# Revit family: Louver-Penthouse-Carnes-Mitered_Corner-PMAB
name_source: partatom
category: Air Terminals
revit_build: Autodesk Revit Architecture 2012 (Build: 20110916_2132(x64)
units: mm (PartAtom-declared; Revit-internal decimal feet)

## types (361) — shared parameters
04 CSI = 08 91 00
1 In 12 Pitched Roof = No
3 in 12 Pitched Roof = Yes
95 CSI = 10200
Assembly Code = D3090700
Blade Material = Aluminum - Carnes - Extruded
Catalog URL = http://www.carnes.com
Connector Description 1 = Duct Connection 1
Custom Length = 220"
Description = Extruded Aluminum Penthouses
Flat Roof = No
Frame Material = Aluminum - Carnes - Extruded
Manufacturer = Carnes Company
Manufacturer Fax = 608-845-6470
Model = PMBA
Pitched Roof Visibility = Yes
Pressure Drop = 0.00 Pa
Product Line = Extruded Aluminum Penthouses
Product Page URL = http://www.carnes.com
Rectangular Length = No
Roof Pitch = 14.04°
Specifications  URL = http://www.carnes.com
Subcategory = Louvers and Dampers
URL = http://www.carnes.com
ecoScorecard Product Page = http://ecoscorecard.com

## per-type parameters (varying)
| type | Blades Length | Blades Quantity | Blades Quantity Control | Blades Width | Free Area | Length Control | Louver Height | Louver Length | Louver Width |
| 12 W x 12 H | 15" | 2 | 2 | 15" | 0.19 SF | 12" | 12" | 12" | 12" |
| 12 W x 18 H | 15" | 4 | 3 | 15" | 0.5 SF | 12" | 18" | 12" | 12" |
| 12 W x 24 H | 15" | 5 | 4 | 15" | 0.77 SF | 12" | 24" | 12" | 12" |
| 12 W x 30 H | 15" | 6 | 5 | 15" | 0.96 SF | 12" | 30" | 12" | 12" |
| 12 W x 36 H | 15" | 7 | 7 | 15" | 1.15 SF | 12" | 36" | 12" | 12" |
| 12 W x 42 H | 15" | 9 | 8 | 15" | 1.43 SF | 12" | 42" | 12" | 12" |
| 12 W x 48 H | 15" | 10 | 9 | 15" | 1.61 SF | 12" | 48" | 12" | 12" |
| 12 W x 54 H | 15" | 11 | 11 | 15" | 1.92 SF | 12" | 54" | 12" | 12" |
| 12 W x 60 H | 15" | 13 | 12 | 15" | 2.11 SF | 12" | 60" | 12" | 12" |
| 12 W x 66 H | 15" | 14 | 13 | 15" | 2.35 SF | 12" | 66" | 12" | 12" |
| 12 W x 72 H | 15" | 15 | 15 | 15" | 2.81 SF | 12" | 72" | 12" | 12" |
| 12 W x 78 H | 15" | 17 | 16 | 15" | 2.88 SF | 12" | 78" | 12" | 12" |
| 12 W x 84 H | 15" | 18 | 17 | 15" | 3.07 SF | 12" | 84" | 12" | 12" |
| 12 W x 90 H | 15" | 19 | 18 | 15" | 3.28 SF | 12" | 90" | 12" | 12" |
| 12 W x 96 H | 15" | 20 | 20 | 15" | 3.55 SF | 12" | 96" | 12" | 12" |
| 12 W x 102 H | 15" | 22 | 21 | 15" | 3.82 SF | 12" | 102" | 12" | 12" |
| 12 W x 108 H | 15" | 23 | 22 | 15" | 3.96 SF | 12" | 108" | 12" | 12" |
| 12 W x 114 H | 15" | 24 | 24 | 15" | 4.24 SF | 12" | 114" | 12" | 12" |
| 12 W x 120 H | 15" | 26 | 25 | 15" | 4.28 SF | 12" | 120" | 12" | 12" |
| 18 W x 12 H | 21" | 2 | 2 | 21" | 0.31 SF | 18" | 12" | 18" | 18" |
| 18 W x 18 H | 21" | 4 | 3 | 21" | 0.8 SF | 18" | 18" | 18" | 18" |
| 18 W x 24 H | 21" | 5 | 4 | 21" | 1.23 SF | 18" | 24" | 18" | 18" |
| 18 W x 30 H | 21" | 6 | 5 | 21" | 1.54 SF | 18" | 30" | 18" | 18" |
| 18 W x 36 H | 21" | 7 | 7 | 21" | 1.85 SF | 18" | 36" | 18" | 18" |
| 18 W x 42 H | 21" | 9 | 8 | 21" | 2.29 SF | 18" | 42" | 18" | 18" |
| 18 W x 48 H | 21" | 10 | 9 | 21" | 2.59 SF | 18" | 48" | 18" | 18" |
| 18 W x 54 H | 21" | 11 | 11 | 21" | 3.09 SF | 18" | 54" | 18" | 18" |
| 18 W x 60 H | 21" | 13 | 12 | 21" | 3.4 SF | 18" | 60" | 18" | 18" |
| 18 W x 66 H | 21" | 14 | 13 | 21" | 3.78 SF | 18" | 66" | 18" | 18" |
| 18 W x 72 H | 21" | 15 | 15 | 21" | 4.52 SF | 18" | 72" | 18" | 18" |
| 18 W x 78 H | 21" | 17 | 16 | 21" | 4.63 SF | 18" | 78" | 18" | 18" |
| 18 W x 84 H | 21" | 18 | 17 | 21" | 4.94 SF | 18" | 84" | 18" | 18" |
| 18 W x 90 H | 21" | 19 | 18 | 21" | 5.27 SF | 18" | 90" | 18" | 18" |
| 18 W x 96 H | 21" | 20 | 20 | 21" | 5.7 SF | 18" | 96" | 18" | 18" |
| 18 W x 102 H | 21" | 22 | 21 | 21" | 6.13 SF | 18" | 102" | 18" | 18" |
| 18 W x 108 H | 21" | 23 | 22 | 21" | 6.37 SF | 18" | 108" | 18" | 18" |
| 18 W x 114 H | 21" | 24 | 24 | 21" | 6.81 SF | 18" | 114" | 18" | 18" |
| 18 W x 120 H | 21" | 26 | 25 | 21" | 6.89 SF | 18" | 120" | 18" | 18" |
| 24 W x 12 H | 27" | 2 | 2 | 27" | 0.43 SF | 24" | 12" | 24" | 24" |
| 24 W x 18 H | 27" | 4 | 3 | 27" | 1.1 SF | 24" | 18" | 24" | 24" |
| 24 W x 24 H | 27" | 5 | 4 | 27" | 1.7 SF | 24" | 24" | 24" | 24" |
| 24 W x 30 H | 27" | 6 | 5 | 27" | 2.13 SF | 24" | 30" | 24" | 24" |
| 24 W x 36 H | 27" | 7 | 7 | 27" | 2.55 SF | 24" | 36" | 24" | 24" |
| 24 W x 42 H | 27" | 9 | 8 | 27" | 3.16 SF | 24" | 42" | 24" | 24" |
| 24 W x 48 H | 27" | 10 | 9 | 27" | 3.57 SF | 24" | 48" | 24" | 24" |
| 24 W x 54 H | 27" | 11 | 11 | 27" | 4.26 SF | 24" | 54" | 24" | 24" |
| 24 W x 60 H | 27" | 13 | 12 | 27" | 4.68 SF | 24" | 60" | 24" | 24" |
| 24 W x 66 H | 27" | 14 | 13 | 27" | 5.21 SF | 24" | 66" | 24" | 24" |
| 24 W x 72 H | 27" | 15 | 15 | 27" | 6.23 SF | 24" | 72" | 24" | 24" |
| 24 W x 78 H | 27" | 17 | 16 | 27" | 6.39 SF | 24" | 78" | 24" | 24" |
| 24 W x 84 H | 27" | 18 | 17 | 27" | 6.81 SF | 24" | 84" | 24" | 24" |
| 24 W x 90 H | 27" | 19 | 18 | 27" | 7.27 SF | 24" | 90" | 24" | 24" |
| 24 W x 96 H | 27" | 20 | 20 | 27" | 7.86 SF | 24" | 96" | 24" | 24" |
| 24 W x 102 H | 27" | 22 | 21 | 27" | 8.45 SF | 24" | 102" | 24" | 24" |
| 24 W x 108 H | 27" | 23 | 22 | 27" | 8.78 SF | 24" | 108" | 24" | 24" |
| 24 W x 114 H | 27" | 24 | 24 | 27" | 9.38 SF | 24" | 114" | 24" | 24" |
| 24 W x 120 H | 27" | 26 | 25 | 27" | 9.49 SF | 24" | 120" | 24" | 24" |
| 30 W x 12 H | 33" | 2 | 2 | 33" | 0.54 SF | 30" | 12" | 30" | 30" |
| 30 W x 18 H | 33" | 4 | 3 | 33" | 1.41 SF | 30" | 18" | 30" | 30" |
| 30 W x 24 H | 33" | 5 | 4 | 33" | 2.16 SF | 30" | 24" | 30" | 30" |
| 30 W x 30 H | 33" | 6 | 5 | 33" | 2.71 SF | 30" | 30" | 30" | 30" |
| 30 W x 36 H | 33" | 7 | 7 | 33" | 3.25 SF | 30" | 36" | 30" | 30" |
| 30 W x 42 H | 33" | 9 | 8 | 33" | 4.02 SF | 30" | 42" | 30" | 30" |
| 30 W x 48 H | 33" | 10 | 9 | 33" | 4.55 SF | 30" | 48" | 30" | 30" |
| 30 W x 54 H | 33" | 11 | 11 | 33" | 5.42 SF | 30" | 54" | 30" | 30" |
| 30 W x 60 H | 33" | 13 | 12 | 33" | 5.97 SF | 30" | 60" | 30" | 30" |
| 30 W x 66 H | 33" | 14 | 13 | 33" | 6.64 SF | 30" | 66" | 30" | 30" |
| 30 W x 72 H | 33" | 15 | 15 | 33" | 7.94 SF | 30" | 72" | 30" | 30" |
| 30 W x 78 H | 33" | 17 | 16 | 33" | 8.14 SF | 30" | 78" | 30" | 30" |
| 30 W x 84 H | 33" | 18 | 17 | 33" | 8.68 SF | 30" | 84" | 30" | 30" |
| 30 W x 90 H | 33" | 19 | 18 | 33" | 9.26 SF | 30" | 90" | 30" | 30" |
| 30 W x 96 H | 33" | 20 | 20 | 33" | 10.02 SF | 30" | 96" | 30" | 30" |
| 30 W x 102 H | 33" | 22 | 21 | 33" | 10.77 SF | 30" | 102" | 30" | 30" |
| 30 W x 108 H | 33" | 23 | 22 | 33" | 11.19 SF | 30" | 108" | 30" | 30" |
| 30 W x 114 H | 33" | 24 | 24 | 33" | 11.96 SF | 30" | 114" | 30" | 30" |
| 30 W x 120 H | 33" | 26 | 25 | 33" | 12.09 SF | 30" | 120" | 30" | 30" |
| 36 W x 12 H | 39" | 2 | 2 | 39" | 0.66 SF | 36" | 12" | 36" | 36" |
| 36 W x 18 H | 39" | 4 | 3 | 39" | 1.71 SF | 36" | 18" | 36" | 36" |
| 36 W x 24 H | 39" | 5 | 4 | 39" | 2.63 SF | 36" | 24" | 36" | 36" |
| 36 W x 30 H | 39" | 6 | 5 | 39" | 3.3 SF | 36" | 30" | 36" | 36" |
| 36 W x 36 H | 39" | 7 | 7 | 39" | 3.96 SF | 36" | 36" | 36" | 36" |
| 36 W x 42 H | 39" | 9 | 8 | 39" | 4.89 SF | 36" | 42" | 36" | 36" |
| 36 W x 48 H | 39" | 10 | 9 | 39" | 5.53 SF | 36" | 48" | 36" | 36" |
| 36 W x 54 H | 39" | 11 | 11 | 39" | 6.59 SF | 36" | 54" | 36" | 36" |
| 36 W x 60 H | 39" | 13 | 12 | 39" | 7.25 SF | 36" | 60" | 36" | 36" |
| 36 W x 66 H | 39" | 14 | 13 | 39" | 8.07 SF | 36" | 66" | 36" | 36" |
| 36 W x 72 H | 39" | 15 | 15 | 39" | 9.65 SF | 36" | 72" | 36" | 36" |
| 36 W x 78 H | 39" | 17 | 16 | 39" | 9.89 SF | 36" | 78" | 36" | 36" |
| 36 W x 84 H | 39" | 18 | 17 | 39" | 10.55 SF | 36" | 84" | 36" | 36" |
| 36 W x 90 H | 39" | 19 | 18 | 39" | 11.25 SF | 36" | 90" | 36" | 36" |
| 36 W x 96 H | 39" | 20 | 20 | 39" | 12.17 SF | 36" | 96" | 36" | 36" |
| 36 W x 102 H | 39" | 22 | 21 | 39" | 13.09 SF | 36" | 102" | 36" | 36" |
| 36 W x 108 H | 39" | 23 | 22 | 39" | 13.6 SF | 36" | 108" | 36" | 36" |
| 36 W x 114 H | 39" | 24 | 24 | 39" | 14.53 SF | 36" | 114" | 36" | 36" |
| 36 W x 120 H | 39" | 26 | 25 | 39" | 14.69 SF | 36" | 120" | 36" | 36" |
| 42 W x 12 H | 45" | 2 | 2 | 45" | 0.78 SF | 42" | 12" | 42" | 42" |
| 42 W x 18 H | 45" | 4 | 3 | 45" | 2.01 SF | 42" | 18" | 42" | 42" |
| 42 W x 24 H | 45" | 5 | 4 | 45" | 3.09 SF | 42" | 24" | 42" | 42" |
| 42 W x 30 H | 45" | 6 | 5 | 45" | 3.88 SF | 42" | 30" | 42" | 42" |
| 42 W x 36 H | 45" | 7 | 7 | 45" | 4.66 SF | 42" | 36" | 42" | 42" |
| 42 W x 42 H | 45" | 9 | 8 | 45" | 5.76 SF | 42" | 42" | 42" | 42" |
| 42 W x 48 H | 45" | 10 | 9 | 45" | 6.51 SF | 42" | 48" | 42" | 42" |
| 42 W x 54 H | 45" | 11 | 11 | 45" | 7.76 SF | 42" | 54" | 42" | 42" |
| 42 W x 60 H | 45" | 13 | 12 | 45" | 8.54 SF | 42" | 60" | 42" | 42" |
| 42 W x 66 H | 45" | 14 | 13 | 45" | 9.5 SF | 42" | 66" | 42" | 42" |
| 42 W x 72 H | 45" | 15 | 15 | 45" | 11.36 SF | 42" | 72" | 42" | 42" |
| 42 W x 78 H | 45" | 17 | 16 | 45" | 11.64 SF | 42" | 78" | 42" | 42" |
| 42 W x 84 H | 45" | 18 | 17 | 45" | 12.42 SF | 42" | 84" | 42" | 42" |
| 42 W x 90 H | 45" | 19 | 18 | 45" | 13.25 SF | 42" | 90" | 42" | 42" |
| 42 W x 96 H | 45" | 20 | 20 | 45" | 14.33 SF | 42" | 96" | 42" | 42" |
| 42 W x 102 H | 45" | 22 | 21 | 45" | 15.41 SF | 42" | 102" | 42" | 42" |
| 42 W x 108 H | 45" | 23 | 22 | 45" | 16.01 SF | 42" | 108" | 42" | 42" |
| 42 W x 114 H | 45" | 24 | 24 | 45" | 17.1 SF | 42" | 114" | 42" | 42" |
| 42 W x 120 H | 45" | 26 | 25 | 45" | 17.3 SF | 42" | 120" | 42" | 42" |
| 48 W x 12 H | 51" | 2 | 2 | 51" | 0.89 SF | 48" | 12" | 48" | 48" |
| 48 W x 18 H | 51" | 4 | 3 | 51" | 2.31 SF | 48" | 18" | 48" | 48" |
| 48 W x 24 H | 51" | 5 | 4 | 51" | 3.56 SF | 48" | 24" | 48" | 48" |
| 48 W x 30 H | 51" | 6 | 5 | 51" | 4.46 SF | 48" | 30" | 48" | 48" |
| 48 W x 36 H | 51" | 7 | 7 | 51" | 5.36 SF | 48" | 36" | 48" | 48" |
| 48 W x 42 H | 51" | 9 | 8 | 51" | 6.62 SF | 48" | 42" | 48" | 48" |
| 48 W x 48 H | 51" | 10 | 9 | 51" | 7.49 SF | 48" | 48" | 48" | 48" |
| 48 W x 54 H | 51" | 11 | 11 | 51" | 8.93 SF | 48" | 54" | 48" | 48" |
| 48 W x 60 H | 51" | 13 | 12 | 51" | 9.82 SF | 48" | 60" | 48" | 48" |
| 48 W x 66 H | 51" | 14 | 13 | 51" | 10.93 SF | 48" | 66" | 48" | 48" |
| 48 W x 72 H | 51" | 15 | 15 | 51" | 13.07 SF | 48" | 72" | 48" | 48" |
| 48 W x 78 H | 51" | 17 | 16 | 51" | 13.39 SF | 48" | 78" | 48" | 48" |
| 48 W x 84 H | 51" | 18 | 17 | 51" | 14.28 SF | 48" | 84" | 48" | 48" |
| 48 W x 90 H | 51" | 19 | 18 | 51" | 15.24 SF | 48" | 90" | 48" | 48" |
| 48 W x 96 H | 51" | 20 | 20 | 51" | 16.48 SF | 48" | 96" | 48" | 48" |
| 48 W x 102 H | 51" | 22 | 21 | 51" | 17.73 SF | 48" | 102" | 48" | 48" |
| 48 W x 108 H | 51" | 23 | 22 | 51" | 18.42 SF | 48" | 108" | 48" | 48" |
| 48 W x 114 H | 51" | 24 | 24 | 51" | 19.68 SF | 48" | 114" | 48" | 48" |
| 48 W x 120 H | 51" | 26 | 25 | 51" | 19.9 SF | 48" | 120" | 48" | 48" |
| 54 W x 12 H | 57" | 2 | 2 | 57" | 1.01 SF | 54" | 12" | 54" | 54" |
| 54 W x 18 H | 57" | 4 | 3 | 57" | 2.62 SF | 54" | 18" | 54" | 54" |
| 54 W x 24 H | 57" | 5 | 4 | 57" | 4.02 SF | 54" | 24" | 54" | 54" |
| 54 W x 30 H | 57" | 6 | 5 | 57" | 5.05 SF | 54" | 30" | 54" | 54" |
| 54 W x 36 H | 57" | 7 | 7 | 57" | 6.06 SF | 54" | 36" | 54" | 54" |
| 54 W x 42 H | 57" | 9 | 8 | 57" | 7.49 SF | 54" | 42" | 54" | 54" |
| 54 W x 48 H | 57" | 10 | 9 | 57" | 8.47 SF | 54" | 48" | 54" | 54" |
| 54 W x 54 H | 57" | 11 | 11 | 57" | 10.1 SF | 54" | 54" | 54" | 54" |
| 54 W x 60 H | 57" | 13 | 12 | 57" | 11.11 SF | 54" | 60" | 54" | 54" |
| 54 W x 66 H | 57" | 14 | 13 | 57" | 12.36 SF | 54" | 66" | 54" | 54" |
| 54 W x 72 H | 57" | 15 | 15 | 57" | 14.78 SF | 54" | 72" | 54" | 54" |
| 54 W x 78 H | 57" | 17 | 16 | 57" | 15.14 SF | 54" | 78" | 54" | 54" |
| 54 W x 84 H | 57" | 18 | 17 | 57" | 16.15 SF | 54" | 84" | 54" | 54" |
| 54 W x 90 H | 57" | 19 | 18 | 57" | 17.23 SF | 54" | 90" | 54" | 54" |
| 54 W x 96 H | 57" | 20 | 20 | 57" | 18.64 SF | 54" | 96" | 54" | 54" |
| 54 W x 102 H | 57" | 22 | 21 | 57" | 20.05 SF | 54" | 102" | 54" | 54" |
| 54 W x 108 H | 57" | 23 | 22 | 57" | 20.82 SF | 54" | 108" | 54" | 54" |
| 54 W x 114 H | 57" | 24 | 24 | 57" | 22.25 SF | 54" | 114" | 54" | 54" |
| 54 W x 120 H | 57" | 26 | 25 | 57" | 22.5 SF | 54" | 120" | 54" | 54" |
| 60 W x 12 H | 63" | 2 | 2 | 63" | 1.13 SF | 60" | 12" | 60" | 60" |
| 60 W x 18 H | 63" | 4 | 3 | 63" | 2.92 SF | 60" | 18" | 60" | 60" |
| 60 W x 24 H | 63" | 5 | 4 | 63" | 4.49 SF | 60" | 24" | 60" | 60" |
| 60 W x 30 H | 63" | 6 | 5 | 63" | 5.63 SF | 60" | 30" | 60" | 60" |
| 60 W x 36 H | 63" | 7 | 7 | 63" | 6.76 SF | 60" | 36" | 60" | 60" |
| 60 W x 42 H | 63" | 9 | 8 | 63" | 8.36 SF | 60" | 42" | 60" | 60" |
| 60 W x 48 H | 63" | 10 | 9 | 63" | 9.45 SF | 60" | 48" | 60" | 60" |
| 60 W x 54 H | 63" | 11 | 11 | 63" | 11.26 SF | 60" | 54" | 60" | 60" |
| 60 W x 60 H | 63" | 13 | 12 | 63" | 12.39 SF | 60" | 60" | 60" | 60" |
| 60 W x 66 H | 63" | 14 | 13 | 63" | 13.79 SF | 60" | 66" | 60" | 60" |
| 60 W x 72 H | 63" | 15 | 15 | 63" | 16.49 SF | 60" | 72" | 60" | 60" |
| 60 W x 78 H | 63" | 17 | 16 | 63" | 16.9 SF | 60" | 78" | 60" | 60" |
| 60 W x 84 H | 63" | 18 | 17 | 63" | 18.02 SF | 60" | 84" | 60" | 60" |
| 60 W x 90 H | 63" | 19 | 18 | 63" | 19.23 SF | 60" | 90" | 60" | 60" |
| 60 W x 96 H | 63" | 20 | 20 | 63" | 20.8 SF | 60" | 96" | 60" | 60" |
| 60 W x 102 H | 63" | 22 | 21 | 63" | 22.36 SF | 60" | 102" | 60" | 60" |
| 60 W x 108 H | 63" | 23 | 22 | 63" | 23.23 SF | 60" | 108" | 60" | 60" |
| 60 W x 114 H | 63" | 24 | 24 | 63" | 24.82 SF | 60" | 114" | 60" | 60" |
| 60 W x 120 H | 63" | 26 | 25 | 63" | 25.1 SF | 60" | 120" | 60" | 60" |
| 66 W x 12 H | 69" | 2 | 2 | 69" | 1.24 SF | 66" | 12" | 66" | 66" |
| 66 W x 18 H | 69" | 4 | 3 | 69" | 3.22 SF | 66" | 18" | 66" | 66" |
| 66 W x 24 H | 69" | 5 | 4 | 69" | 4.96 SF | 66" | 24" | 66" | 66" |
| 66 W x 30 H | 69" | 6 | 5 | 69" | 6.22 SF | 66" | 30" | 66" | 66" |
| 66 W x 36 H | 69" | 7 | 7 | 69" | 7.46 SF | 66" | 36" | 66" | 66" |
| 66 W x 42 H | 69" | 9 | 8 | 69" | 9.22 SF | 66" | 42" | 66" | 66" |
| 66 W x 48 H | 69" | 10 | 9 | 69" | 10.43 SF | 66" | 48" | 66" | 66" |
| 66 W x 54 H | 69" | 11 | 11 | 69" | 12.43 SF | 66" | 54" | 66" | 66" |
| 66 W x 60 H | 69" | 13 | 12 | 69" | 13.67 SF | 66" | 60" | 66" | 66" |
| 66 W x 66 H | 69" | 14 | 13 | 69" | 15.22 SF | 66" | 66" | 66" | 66" |
| 66 W x 72 H | 69" | 15 | 15 | 69" | 18.2 SF | 66" | 72" | 66" | 66" |
| 66 W x 78 H | 69" | 17 | 16 | 69" | 18.65 SF | 66" | 78" | 66" | 66" |
| 66 W x 84 H | 69" | 18 | 17 | 69" | 19.89 SF | 66" | 84" | 66" | 66" |
| 66 W x 90 H | 69" | 19 | 18 | 69" | 21.22 SF | 66" | 90" | 66" | 66" |
| 66 W x 96 H | 69" | 20 | 20 | 69" | 22.95 SF | 66" | 96" | 66" | 66" |
| 66 W x 102 H | 69" | 22 | 21 | 69" | 24.68 SF | 66" | 102" | 66" | 66" |
| 66 W x 108 H | 69" | 23 | 22 | 69" | 25.64 SF | 66" | 108" | 66" | 66" |
| 66 W x 114 H | 69" | 24 | 24 | 69" | 27.4 SF | 66" | 114" | 66" | 66" |
| 66 W x 120 H | 69" | 26 | 25 | 69" | 27.71 SF | 66" | 120" | 66" | 66" |
| 72 W x 12 H | 75" | 2 | 2 | 75" | 1.36 SF | 72" | 12" | 72" | 72" |
| 72 W x 18 H | 75" | 4 | 3 | 75" | 3.53 SF | 72" | 18" | 72" | 72" |
| 72 W x 24 H | 75" | 5 | 4 | 75" | 5.42 SF | 72" | 24" | 72" | 72" |
| 72 W x 30 H | 75" | 6 | 5 | 75" | 6.8 SF | 72" | 30" | 72" | 72" |
| 72 W x 36 H | 75" | 7 | 7 | 75" | 8.16 SF | 72" | 36" | 72" | 72" |
| 72 W x 42 H | 75" | 9 | 8 | 75" | 10.09 SF | 72" | 42" | 72" | 72" |
| 72 W x 48 H | 75" | 10 | 9 | 75" | 11.41 SF | 72" | 48" | 72" | 72" |
| 72 W x 54 H | 75" | 11 | 11 | 75" | 13.6 SF | 72" | 54" | 72" | 72" |
| 72 W x 60 H | 75" | 13 | 12 | 75" | 14.96 SF | 72" | 60" | 72" | 72" |
| 72 W x 66 H | 75" | 14 | 13 | 75" | 16.65 SF | 72" | 66" | 72" | 72" |
| 72 W x 72 H | 75" | 15 | 15 | 75" | 19.9 SF | 72" | 72" | 72" | 72" |
| 72 W x 78 H | 75" | 17 | 16 | 75" | 20.4 SF | 72" | 78" | 72" | 72" |
| 72 W x 84 H | 75" | 18 | 17 | 75" | 21.76 SF | 72" | 84" | 72" | 72" |
| 72 W x 90 H | 75" | 19 | 18 | 75" | 23.21 SF | 72" | 90" | 72" | 72" |
| 72 W x 96 H | 75" | 20 | 20 | 75" | 25.11 SF | 72" | 96" | 72" | 72" |
| 72 W x 102 H | 75" | 22 | 21 | 75" | 27 SF | 72" | 102" | 72" | 72" |
| 72 W x 108 H | 75" | 23 | 22 | 75" | 28.05 SF | 72" | 108" | 72" | 72" |
| 72 W x 114 H | 75" | 24 | 24 | 75" | 29.97 SF | 72" | 114" | 72" | 72" |
| 72 W x 120 H | 75" | 26 | 25 | 75" | 30.31 SF | 72" | 120" | 72" | 72" |
| 78 W x 12 H | 81" | 2 | 2 | 81" | 1.48 SF | 78" | 12" | 78" | 78" |
| 78 W x 18 H | 81" | 4 | 3 | 81" | 3.83 SF | 78" | 18" | 78" | 78" |
| 78 W x 24 H | 81" | 5 | 4 | 81" | 5.89 SF | 78" | 24" | 78" | 78" |
| 78 W x 30 H | 81" | 6 | 5 | 81" | 7.38 SF | 78" | 30" | 78" | 78" |
| 78 W x 36 H | 81" | 7 | 7 | 81" | 8.86 SF | 78" | 36" | 78" | 78" |
| 78 W x 42 H | 81" | 9 | 8 | 81" | 10.95 SF | 78" | 42" | 78" | 78" |
| 78 W x 48 H | 81" | 10 | 9 | 81" | 12.39 SF | 78" | 48" | 78" | 78" |
| 78 W x 54 H | 81" | 11 | 11 | 81" | 14.77 SF | 78" | 54" | 78" | 78" |
| 78 W x 60 H | 81" | 13 | 12 | 81" | 16.24 SF | 78" | 60" | 78" | 78" |
| 78 W x 66 H | 81" | 14 | 13 | 81" | 18.08 SF | 78" | 66" | 78" | 78" |
| 78 W x 72 H | 81" | 15 | 15 | 81" | 21.61 SF | 78" | 72" | 78" | 78" |
| 78 W x 78 H | 81" | 17 | 16 | 81" | 22.15 SF | 78" | 78" | 78" | 78" |
| 78 W x 84 H | 81" | 18 | 17 | 81" | 23.63 SF | 78" | 84" | 78" | 78" |
| 78 W x 90 H | 81" | 19 | 18 | 81" | 25.21 SF | 78" | 90" | 78" | 78" |
| 78 W x 96 H | 81" | 20 | 20 | 81" | 27.26 SF | 78" | 96" | 78" | 78" |
| 78 W x 102 H | 81" | 22 | 21 | 81" | 29.32 SF | 78" | 102" | 78" | 78" |
| 78 W x 108 H | 81" | 23 | 22 | 81" | 30.46 SF | 78" | 108" | 78" | 78" |
| 78 W x 114 H | 81" | 24 | 24 | 81" | 32.54 SF | 78" | 114" | 78" | 78" |
| 78 W x 120 H | 81" | 26 | 25 | 81" | 32.91 SF | 78" | 120" | 78" | 78" |
| 84 W x 12 H | 87" | 2 | 2 | 87" | 1.59 SF | 84" | 12" | 84" | 84" |
| 84 W x 18 H | 87" | 4 | 3 | 87" | 4.13 SF | 84" | 18" | 84" | 84" |
| 84 W x 24 H | 87" | 5 | 4 | 87" | 6.35 SF | 84" | 24" | 84" | 84" |
| 84 W x 30 H | 87" | 6 | 5 | 87" | 7.97 SF | 84" | 30" | 84" | 84" |
| 84 W x 36 H | 87" | 7 | 7 | 87" | 9.56 SF | 84" | 36" | 84" | 84" |
| 84 W x 42 H | 87" | 9 | 8 | 87" | 11.82 SF | 84" | 42" | 84" | 84" |
| 84 W x 48 H | 87" | 10 | 9 | 87" | 13.37 SF | 84" | 48" | 84" | 84" |
| 84 W x 54 H | 87" | 11 | 11 | 87" | 15.93 SF | 84" | 54" | 84" | 84" |
| 84 W x 60 H | 87" | 13 | 12 | 87" | 17.53 SF | 84" | 60" | 84" | 84" |
| 84 W x 66 H | 87" | 14 | 13 | 87" | 19.51 SF | 84" | 66" | 84" | 84" |
| 84 W x 72 H | 87" | 15 | 15 | 87" | 23.32 SF | 84" | 72" | 84" | 84" |
| 84 W x 78 H | 87" | 17 | 16 | 87" | 23.9 SF | 84" | 78" | 84" | 84" |
| 84 W x 84 H | 87" | 18 | 17 | 87" | 25.49 SF | 84" | 84" | 84" | 84" |
| 84 W x 90 H | 87" | 19 | 18 | 87" | 27.2 SF | 84" | 90" | 84" | 84" |
| 84 W x 96 H | 87" | 20 | 20 | 87" | 29.42 SF | 84" | 96" | 84" | 84" |
| 84 W x 102 H | 87" | 22 | 21 | 87" | 31.64 SF | 84" | 102" | 84" | 84" |
| 84 W x 108 H | 87" | 23 | 22 | 87" | 32.87 SF | 84" | 108" | 84" | 84" |
| 84 W x 114 H | 87" | 24 | 24 | 87" | 35.12 SF | 84" | 114" | 84" | 84" |
| 84 W x 120 H | 87" | 26 | 25 | 87" | 35.51 SF | 84" | 120" | 84" | 84" |
| 90 W x 12 H | 93" | 2 | 2 | 93" | 1.71 SF | 90" | 12" | 90" | 90" |
| 90 W x 18 H | 93" | 4 | 3 | 93" | 4.43 SF | 90" | 18" | 90" | 90" |
| 90 W x 24 H | 93" | 5 | 4 | 93" | 6.82 SF | 90" | 24" | 90" | 90" |
| 90 W x 30 H | 93" | 6 | 5 | 93" | 8.55 SF | 90" | 30" | 90" | 90" |
| 90 W x 36 H | 93" | 7 | 7 | 93" | 10.26 SF | 90" | 36" | 90" | 90" |
| 90 W x 42 H | 93" | 9 | 8 | 93" | 12.69 SF | 90" | 42" | 90" | 90" |
| 90 W x 48 H | 93" | 10 | 9 | 93" | 14.35 SF | 90" | 48" | 90" | 90" |
| 90 W x 54 H | 93" | 11 | 11 | 93" | 17.1 SF | 90" | 54" | 90" | 90" |
| 90 W x 60 H | 93" | 13 | 12 | 93" | 18.81 SF | 90" | 60" | 90" | 90" |
| 90 W x 66 H | 93" | 14 | 13 | 93" | 20.94 SF | 90" | 66" | 90" | 90" |
| 90 W x 72 H | 93" | 15 | 15 | 93" | 25.03 SF | 90" | 72" | 90" | 90" |
| 90 W x 78 H | 93" | 17 | 16 | 93" | 25.65 SF | 90" | 78" | 90" | 90" |
| 90 W x 84 H | 93" | 18 | 17 | 93" | 27.36 SF | 90" | 84" | 90" | 90" |
| 90 W x 90 H | 93" | 19 | 18 | 93" | 29.19 SF | 90" | 90" | 90" | 90" |
| 90 W x 96 H | 93" | 20 | 20 | 93" | 31.57 SF | 90" | 96" | 90" | 90" |
| 90 W x 102 H | 93" | 22 | 21 | 93" | 33.96 SF | 90" | 102" | 90" | 90" |
| 90 W x 108 H | 93" | 23 | 22 | 93" | 35.28 SF | 90" | 108" | 90" | 90" |
| 90 W x 114 H | 93" | 24 | 24 | 93" | 37.69 SF | 90" | 114" | 90" | 90" |
| 90 W x 120 H | 93" | 26 | 25 | 93" | 38.12 SF | 90" | 120" | 90" | 90" |
| 96 W x 12 H | 99" | 2 | 2 | 99" | 1.83 SF | 96" | 12" | 96" | 96" |
| 96 W x 18 H | 99" | 4 | 3 | 99" | 4.74 SF | 96" | 18" | 96" | 96" |
| 96 W x 24 H | 99" | 5 | 4 | 99" | 7.28 SF | 96" | 24" | 96" | 96" |
| 96 W x 30 H | 99" | 6 | 5 | 99" | 9.13 SF | 96" | 30" | 96" | 96" |
| 96 W x 36 H | 99" | 7 | 7 | 99" | 10.96 SF | 96" | 36" | 96" | 96" |
| 96 W x 42 H | 99" | 9 | 8 | 99" | 13.55 SF | 96" | 42" | 96" | 96" |
| 96 W x 48 H | 99" | 10 | 9 | 99" | 15.33 SF | 96" | 48" | 96" | 96" |
| 96 W x 54 H | 99" | 11 | 11 | 99" | 18.27 SF | 96" | 54" | 96" | 96" |
| 96 W x 60 H | 99" | 13 | 12 | 99" | 20.1 SF | 96" | 60" | 96" | 96" |
| 96 W x 66 H | 99" | 14 | 13 | 99" | 22.37 SF | 96" | 66" | 96" | 96" |
| 96 W x 72 H | 99" | 15 | 15 | 99" | 26.74 SF | 96" | 72" | 96" | 96" |
| 96 W x 78 H | 99" | 17 | 16 | 99" | 27.4 SF | 96" | 78" | 96" | 96" |
| 96 W x 84 H | 99" | 18 | 17 | 99" | 29.23 SF | 96" | 84" | 96" | 96" |
| 96 W x 90 H | 99" | 19 | 18 | 99" | 31.18 SF | 96" | 90" | 96" | 96" |
| 96 W x 96 H | 99" | 20 | 20 | 99" | 33.73 SF | 96" | 96" | 96" | 96" |
| 96 W x 102 H | 99" | 22 | 21 | 99" | 36.28 SF | 96" | 102" | 96" | 96" |
| 96 W x 108 H | 99" | 23 | 22 | 99" | 37.68 SF | 96" | 108" | 96" | 96" |
| 96 W x 114 H | 99" | 24 | 24 | 99" | 40.26 SF | 96" | 114" | 96" | 96" |
| 96 W x 120 H | 99" | 26 | 25 | 99" | 40.72 SF | 96" | 120" | 96" | 96" |
| 102 W x 12 H | 105" | 2 | 2 | 105" | 1.94 SF | 102" | 12" | 102" | 102" |
| 102 W x 18 H | 105" | 4 | 3 | 105" | 5.04 SF | 102" | 18" | 102" | 102" |
| 102 W x 24 H | 105" | 5 | 4 | 105" | 7.75 SF | 102" | 24" | 102" | 102" |
| 102 W x 30 H | 105" | 6 | 5 | 105" | 9.72 SF | 102" | 30" | 102" | 102" |
| 102 W x 36 H | 105" | 7 | 7 | 105" | 11.66 SF | 102" | 36" | 102" | 102" |
| 102 W x 42 H | 105" | 9 | 8 | 105" | 14.42 SF | 102" | 42" | 102" | 102" |
| 102 W x 48 H | 105" | 10 | 9 | 105" | 16.31 SF | 102" | 48" | 102" | 102" |
| 102 W x 54 H | 105" | 11 | 11 | 105" | 19.44 SF | 102" | 54" | 102" | 102" |
| 102 W x 60 H | 105" | 13 | 12 | 105" | 21.38 SF | 102" | 60" | 102" | 102" |
| 102 W x 66 H | 105" | 14 | 13 | 105" | 23.8 SF | 102" | 66" | 102" | 102" |
| 102 W x 72 H | 105" | 15 | 15 | 105" | 28.45 SF | 102" | 72" | 102" | 102" |
| 102 W x 78 H | 105" | 17 | 16 | 105" | 29.16 SF | 102" | 78" | 102" | 102" |
| 102 W x 84 H | 105" | 18 | 17 | 105" | 31.1 SF | 102" | 84" | 102" | 102" |
| 102 W x 90 H | 105" | 19 | 18 | 105" | 33.18 SF | 102" | 90" | 102" | 102" |
| 102 W x 96 H | 105" | 20 | 20 | 105" | 35.89 SF | 102" | 96" | 102" | 102" |
| 102 W x 102 H | 105" | 22 | 21 | 105" | 38.59 SF | 102" | 102" | 102" | 102" |
| 102 W x 108 H | 105" | 23 | 22 | 105" | 40.09 SF | 102" | 108" | 102" | 102" |
| 102 W x 114 H | 105" | 24 | 24 | 105" | 42.84 SF | 102" | 114" | 102" | 102" |
| 102 W x 120 H | 105" | 26 | 25 | 105" | 43.32 SF | 102" | 120" | 102" | 102" |
| 108 W x 12 H | 111" | 2 | 2 | 111" | 2.06 SF | 108" | 12" | 108" | 108" |
| 108 W x 18 H | 111" | 4 | 3 | 111" | 5.34 SF | 108" | 18" | 108" | 108" |
| 108 W x 24 H | 111" | 5 | 4 | 111" | 8.21 SF | 108" | 24" | 108" | 108" |
| 108 W x 30 H | 111" | 6 | 5 | 111" | 10.3 SF | 108" | 30" | 108" | 108" |
| 108 W x 36 H | 111" | 7 | 7 | 111" | 12.36 SF | 108" | 36" | 108" | 108" |
| 108 W x 42 H | 111" | 9 | 8 | 111" | 15.29 SF | 108" | 42" | 108" | 108" |
| 108 W x 48 H | 111" | 10 | 9 | 111" | 17.29 SF | 108" | 48" | 108" | 108" |
| 108 W x 54 H | 111" | 11 | 11 | 111" | 20.61 SF | 108" | 54" | 108" | 108" |
| 108 W x 60 H | 111" | 13 | 12 | 111" | 22.67 SF | 108" | 60" | 108" | 108" |
| 108 W x 66 H | 111" | 14 | 13 | 111" | 25.23 SF | 108" | 66" | 108" | 108" |
| 108 W x 72 H | 111" | 15 | 15 | 111" | 30.16 SF | 108" | 72" | 108" | 108" |
| 108 W x 78 H | 111" | 17 | 16 | 111" | 30.91 SF | 108" | 78" | 108" | 108" |
| 108 W x 84 H | 111" | 18 | 17 | 111" | 32.97 SF | 108" | 84" | 108" | 108" |
| 108 W x 90 H | 111" | 19 | 18 | 111" | 35.17 SF | 108" | 90" | 108" | 108" |
| 108 W x 96 H | 111" | 20 | 20 | 111" | 38.04 SF | 108" | 96" | 108" | 108" |
| 108 W x 102 H | 111" | 22 | 21 | 111" | 40.91 SF | 108" | 102" | 108" | 108" |
| 108 W x 108 H | 111" | 23 | 22 | 111" | 42.5 SF | 108" | 108" | 108" | 108" |
| 108 W x 114 H | 111" | 24 | 24 | 111" | 45.41 SF | 108" | 114" | 108" | 108" |
| 108 W x 120 H | 111" | 26 | 25 | 111" | 45.92 SF | 108" | 120" | 108" | 108" |
| 114 W x 12 H | 117" | 2 | 2 | 117" | 2.18 SF | 114" | 12" | 114" | 114" |
| 114 W x 18 H | 117" | 4 | 3 | 117" | 5.65 SF | 114" | 18" | 114" | 114" |
| 114 W x 24 H | 117" | 5 | 4 | 117" | 8.68 SF | 114" | 24" | 114" | 114" |
| 114 W x 30 H | 117" | 6 | 5 | 117" | 10.89 SF | 114" | 30" | 114" | 114" |
| 114 W x 36 H | 117" | 7 | 7 | 117" | 13.06 SF | 114" | 36" | 114" | 114" |
| 114 W x 42 H | 117" | 9 | 8 | 117" | 16.15 SF | 114" | 42" | 114" | 114" |
| 114 W x 48 H | 117" | 10 | 9 | 117" | 18.27 SF | 114" | 48" | 114" | 114" |
| 114 W x 54 H | 117" | 11 | 11 | 117" | 21.77 SF | 114" | 54" | 114" | 114" |
| 114 W x 60 H | 117" | 13 | 12 | 117" | 23.95 SF | 114" | 60" | 114" | 114" |
| 114 W x 66 H | 117" | 14 | 13 | 117" | 26.66 SF | 114" | 66" | 114" | 114" |
| 114 W x 72 H | 117" | 15 | 15 | 117" | 31.87 SF | 114" | 72" | 114" | 114" |
| 114 W x 78 H | 117" | 17 | 16 | 117" | 32.66 SF | 114" | 78" | 114" | 114" |
| 114 W x 84 H | 117" | 18 | 17 | 117" | 34.84 SF | 114" | 84" | 114" | 114" |
| 114 W x 90 H | 117" | 19 | 18 | 117" | 37.16 SF | 114" | 90" | 114" | 114" |
| 114 W x 96 H | 117" | 20 | 20 | 117" | 40.2 SF | 114" | 96" | 114" | 114" |
| 114 W x 102 H | 117" | 22 | 21 | 117" | 43.23 SF | 114" | 102" | 114" | 114" |
| 114 W x 108 H | 117" | 23 | 22 | 117" | 44.91 SF | 114" | 108" | 114" | 114" |
| 114 W x 114 H | 117" | 24 | 24 | 117" | 47.98 SF | 114" | 114" | 114" | 114" |
| 114 W x 120 H | 117" | 26 | 25 | 117" | 48.53 SF | 114" | 120" | 114" | 114" |
| 120 W x 12 H | 123" | 2 | 2 | 123" | 2.29 SF | 120" | 12" | 120" | 120" |
| 120 W x 18 H | 123" | 4 | 3 | 123" | 5.95 SF | 120" | 18" | 120" | 120" |
| 120 W x 24 H | 123" | 5 | 4 | 123" | 9.14 SF | 120" | 24" | 120" | 120" |
| 120 W x 30 H | 123" | 6 | 5 | 123" | 11.47 SF | 120" | 30" | 120" | 120" |
| 120 W x 36 H | 123" | 7 | 7 | 123" | 13.76 SF | 120" | 36" | 120" | 120" |
| 120 W x 42 H | 123" | 9 | 8 | 123" | 17.02 SF | 120" | 42" | 120" | 120" |
| 120 W x 48 H | 123" | 10 | 9 | 123" | 19.25 SF | 120" | 48" | 120" | 120" |
| 120 W x 54 H | 123" | 11 | 11 | 123" | 22.94 SF | 120" | 54" | 120" | 120" |
| 120 W x 60 H | 123" | 13 | 12 | 123" | 25.23 SF | 120" | 60" | 120" | 120" |
| 120 W x 66 H | 123" | 14 | 13 | 123" | 28.09 SF | 120" | 66" | 120" | 120" |
| 120 W x 72 H | 123" | 15 | 15 | 123" | 33.58 SF | 120" | 72" | 120" | 120" |
| 120 W x 78 H | 123" | 17 | 16 | 123" | 34.41 SF | 120" | 78" | 120" | 120" |
| 120 W x 84 H | 123" | 18 | 17 | 123" | 36.7 SF | 120" | 84" | 120" | 120" |
| 120 W x 90 H | 123" | 19 | 18 | 123" | 39.16 SF | 120" | 90" | 120" | 120" |
| 120 W x 96 H | 123" | 20 | 20 | 123" | 42.35 SF | 120" | 96" | 120" | 120" |
| 120 W x 102 H | 123" | 22 | 21 | 123" | 45.55 SF | 120" | 102" | 120" | 120" |
| 120 W x 108 H | 123" | 23 | 22 | 123" | 47.32 SF | 120" | 108" | 120" | 120" |
| 120 W x 114 H | 123" | 24 | 24 | 123" | 50.56 SF | 120" | 114" | 120" | 120" |
| 120 W x 120 H | 123" | 26 | 25 | 123" | 51.13 SF | 120" | 120" | 120" | 120" |

## geometry (parser evidence)
native form markers: Blend x6, Sweep x3
no freeform markers — native parametric forms only
